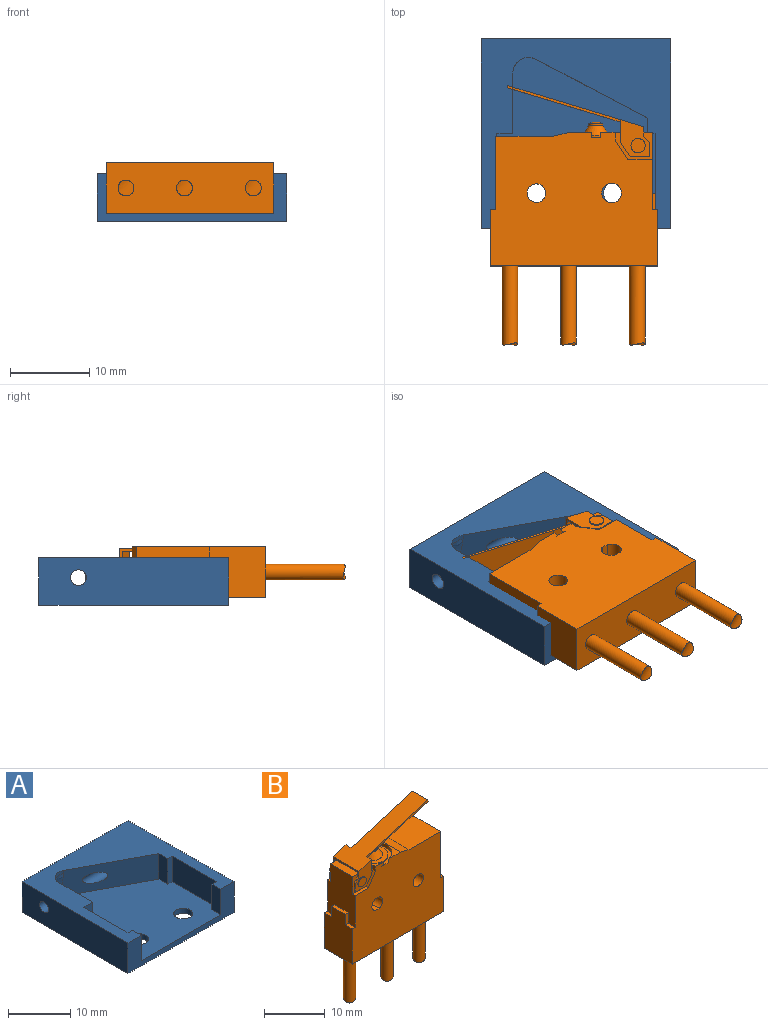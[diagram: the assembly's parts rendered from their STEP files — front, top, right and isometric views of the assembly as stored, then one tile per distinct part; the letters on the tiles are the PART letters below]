
ASSEMBLY  parts=2 mates=1
PART A: 27 faces, bbox 24.8x24.8x7.2 mm
  f0: plane 24x24mm, normal (0,0,1), area 232mm2, adj f4,f5,f6,f10,f11,f12,f13,f14
  f1: cylinder r=1mm len=3mm, axis (1,0,0), area 18.8mm2, adj f4,f22
  f2: cylinder r=1mm len=13.34mm, axis (1,0,0), area 72.3mm2, adj f21,f23
  f3: plane 21.68x20mm, normal (0,0,1), area 329.8mm2, adj f5,f7,f8,f10,f11,f12,f13,f14
  f4: plane 24x6mm, normal (-1,0,0), area 140.9mm2, adj f0,f1,f5,f9,f20
  f5: plane 24x6mm, normal (0,-1,0), area 54mm2, adj f0,f3,f4,f6,f9,f14,f15
  f6: plane 24x6mm, normal (1,0,0), area 131.4mm2, adj f0,f5,f9,f20,f23
  f7: cylinder r=1.5mm len=3mm, axis (0,0,1), area 9.4mm2, adj f3,f9
  f8: cylinder r=1.5mm len=3mm, axis (0,0,1), area 9.4mm2, adj f3,f9
  f9: plane 24x24mm, normal (0,0,-1), area 561.9mm2, adj f4,f5,f6,f7,f8,f20
  f10: plane 5x2mm, normal (-1,0,0), area 10mm2, adj f0,f3,f11,f21
  f11: plane 5x1mm, normal (0,-1,0), area 5mm2, adj f0,f3,f10,f12
  f12: plane 10x5mm, normal (-1,0,0), area 50mm2, adj f0,f3,f11,f13
  f13: plane 5x1mm, normal (0,1,0), area 5mm2, adj f0,f3,f12,f14
  f14: plane 5x2mm, normal (-1,0,0), area 10mm2, adj f0,f3,f5,f13
  f15: plane 5x2mm, normal (1,0,0), area 10mm2, adj f0,f3,f5,f16
  f16: plane 5x1mm, normal (0,1,0), area 5mm2, adj f0,f3,f15,f17
  f17: plane 10x5mm, normal (1,0,0), area 50mm2, adj f0,f3,f16,f18
  f18: plane 5x2mm, normal (0,-1,0), area 10mm2, adj f0,f3,f17,f19
  f19: plane 7.68x5mm, normal (1,0,0), area 29.4mm2, adj f0,f3,f18,f22,f24,f26
  f20: plane 24x6mm, normal (0,1,0), area 144mm2, adj f0,f4,f6,f9
  f21: plane 15.11x8.37mm, normal (-0.47,-0.88,0), area 73.4mm2, adj f0,f2,f3,f10,f24,f25,f26
  f22: torus R=2mm, axis (1,0,0), area 12mm2, adj f1,f19,f25
  f23: torus R=2mm, axis (1,0,0), area 13.5mm2, adj f2,f6
  f24: cylinder r=2mm len=2.94mm, axis (0,0,-1), area 2.5mm2, adj f0,f19,f21,f25
  f25: bspline ~4.52x3.47mm, area 13.7mm2, adj f21,f22,f24,f26
  f26: cylinder r=2mm len=2.94mm, axis (0,0,-1), area 2.5mm2, adj f3,f19,f21,f25
PART B: 76 faces, bbox 21.2x6.4x32.8 mm
  f0: cylinder r=3.25mm len=6.4mm, axis (0,0,1), area 6.3mm2, adj f53,f71,f72,f75
  f1: cylinder r=3.25mm len=6.4mm, axis (0,0,1), area 6.3mm2, adj f53,f63,f71,f75
  f2: cylinder r=0.9mm len=1.8mm, axis (0,0,1), area 1.6mm2, adj f3,f70
  f3: cone r=1.3mm half-angle=33.7deg, axis (0,0,-1), area 11.8mm2, adj f2,f69
  f4: cylinder r=2.6mm len=5.2mm, axis (0,0,1), area 4.9mm2, adj f69,f71
  f5: cylinder r=0.9mm len=1.8mm, axis (0,-1,0), area 0.3mm2, adj f19,f65
  f6: cylinder r=0.9mm len=1.8mm, axis (0,-1,0), area 0.8mm2, adj f18,f57
  f7: cylinder r=1.25mm len=6.4mm, axis (0,1,0), area 19.6mm2, adj f53,f55,f56,f75
  f8: cylinder r=1.25mm len=6.4mm, axis (0,1,0), area 19.6mm2, adj f53,f55,f56,f75
  f9: cylinder r=1.18mm len=6.4mm, axis (0,1,0), area 47.2mm2, adj f53,f75
  f10: cylinder r=2mm len=2.83mm, axis (0.71,-0.71,0), area 2.5mm2, adj f11
  f11: cylinder r=1mm len=10mm, axis (0,0,-1), area 62mm2, adj f10,f52
  f12: cylinder r=2mm len=2.83mm, axis (0.71,-0.71,0), area 2.5mm2, adj f13
  f13: cylinder r=1mm len=10mm, axis (0,0,-1), area 62mm2, adj f12,f52
  f14: cylinder r=2mm len=2.83mm, axis (0.71,-0.71,0), area 2.5mm2, adj f15
  f15: cylinder r=1mm len=10mm, axis (0,0,-1), area 62mm2, adj f14,f52
  f16: cylinder r=0.9mm len=1.8mm, axis (0,-1,0), area 0.8mm2, adj f21,f58
  f17: cylinder r=0.9mm len=1.8mm, axis (0,-1,0), area 0.3mm2, adj f20,f60
  f18: plane 4.69x3.75mm, normal (0,1,0), area 10.6mm2, adj f6,f25,f29,f31,f33,f35,f37,f39
  f19: plane 4.38x3.75mm, normal (0,1,0), area 9.7mm2, adj f5,f28,f30,f32,f34,f36,f38,f39
  f20: plane 4.38x3.75mm, normal (0,-1,0), area 9.7mm2, adj f17,f28,f29,f31,f33,f35,f37,f39
  f21: plane 4.69x3.75mm, normal (0,-1,0), area 10.6mm2, adj f16,f25,f30,f32,f34,f36,f38,f39
  f22: plane 14.29x4.62mm, normal (0,1,0), area 4.5mm2, adj f23,f24,f25,f27,f28,f37
  f23: plane 12.4x3.76mm, normal (0.29,0,-0.96), area 46.6mm2, adj f22,f24,f26,f27
  f24: plane 3.6x0.29mm, normal (0.96,0,0.29), area 1.1mm2, adj f22,f23,f25,f26
  f25: plane 17.15x5.9mm, normal (-0.29,0,0.96), area 71.6mm2, adj f18,f21,f22,f24,f26,f37,f38,f39
  f26: plane 14.29x4.62mm, normal (0,-1,0), area 4.5mm2, adj f23,f24,f25,f27,f28,f38
  f27: plane 3.6x0mm, normal (-0.96,0,-0.29), area 0mm2, adj f22,f23,f26,f28
  f28: plane 5.3x4.84mm, normal (0.29,0,-0.96), area 23.5mm2, adj f19,f20,f22,f26,f27,f37,f38,f39
  f29: plane 0.8x0.8mm, normal (-0.71,0,0.71), area 0.3mm2, adj f18,f20,f31,f39
  f30: plane 0.8x0.8mm, normal (-0.71,0,0.71), area 0.3mm2, adj f19,f21,f32,f39
  f31: plane 1.8x0.3mm, normal (-1,0,0), area 0.5mm2, adj f18,f20,f29,f33
  f32: plane 1.8x0.3mm, normal (-1,0,0), area 0.5mm2, adj f19,f21,f30,f34
  f33: plane 2.5x0.3mm, normal (0,0,-1), area 0.7mm2, adj f18,f20,f31,f35
  f34: plane 2.5x0.3mm, normal (0,0,-1), area 0.7mm2, adj f19,f21,f32,f36
  f35: plane 1.79x1.25mm, normal (0.82,0,-0.57), area 0.7mm2, adj f18,f20,f33,f37
  f36: plane 1.79x1.25mm, normal (0.82,0,-0.57), area 0.7mm2, adj f19,f21,f34,f38
  f37: plane 2.91x1.15mm, normal (1,0,0), area 1.1mm2, adj f18,f20,f22,f25,f28,f35
  f38: plane 2.91x1.15mm, normal (1,0,0), area 1.1mm2, adj f19,f21,f25,f26,f28,f36
  f39: plane 5.9x1.2mm, normal (-1,0,0), area 2.4mm2, adj f18,f19,f20,f21,f25,f28,f29,f30
  f40: plane 2.1x0.7mm, normal (0,-1,0), area 1.5mm2, adj f41,f46,f51,f64
  f41: plane 3.2x0.7mm, normal (0,0,1), area 2.2mm2, adj f40,f42,f51,f64
  f42: plane 2.1x0.7mm, normal (0,1,0), area 1.5mm2, adj f41,f43,f51,f64
  f43: plane 1.6x0.7mm, normal (0,0,1), area 1.1mm2, adj f42,f51,f64,f75
  f44: plane 1.6x0.7mm, normal (0,0,1), area 1.1mm2, adj f47,f50,f54,f75
  f45: plane 1.6x0.7mm, normal (0,0,1), area 1.1mm2, adj f48,f50,f53,f54
  f46: plane 1.6x0.7mm, normal (0,0,1), area 1.1mm2, adj f40,f51,f53,f64
  f47: plane 2.1x0.7mm, normal (0,1,0), area 1.5mm2, adj f44,f49,f50,f54
  f48: plane 2.1x0.7mm, normal (0,-1,0), area 1.5mm2, adj f45,f49,f50,f54
  f49: plane 3.2x0.7mm, normal (0,0,1), area 2.2mm2, adj f47,f48,f50,f54
  f50: plane 9.2x6.4mm, normal (1,0,0), area 52.2mm2, adj f44,f45,f47,f48,f49,f52,f53,f75
  f51: plane 9.2x6.4mm, normal (-1,0,0), area 52.2mm2, adj f40,f41,f42,f43,f46,f52,f53,f75
  f52: plane 21.2x6.4mm, normal (0,0,-1), area 126.3mm2, adj f11,f13,f15,f50,f51,f53,f75
  f53: plane 21.2x16.9mm, normal (0,-1,0), area 316mm2, adj f0,f1,f7,f8,f9,f45,f46,f50
  f54: plane 9.3x6.4mm, normal (1,0,0), area 52.8mm2, adj f44,f45,f47,f48,f49,f53,f74,f75
  f55: plane 6.4x0.85mm, normal (0,0,1), area 5.5mm2, adj f7,f8,f53,f75
  f56: plane 6.4x0.85mm, normal (0,0,-1), area 5.5mm2, adj f7,f8,f53,f75
  f57: plane 1.8x1.8mm, normal (0,1,0), area 2.5mm2, adj f6
  f58: plane 1.8x1.8mm, normal (0,-1,0), area 2.5mm2, adj f16
  f59: plane 1x0.6mm, normal (-1,0,0), area 0.6mm2, adj f60,f61,f63,f75
  f60: plane 4.7x3.5mm, normal (0,1,0), area 11.9mm2, adj f17,f59,f61,f62,f63,f64
  f61: plane 2.5x1.6mm, normal (-0.84,0,0.54), area 1.8mm2, adj f59,f60,f62,f75
  f62: plane 3.1x0.6mm, normal (0,0,1), area 1.9mm2, adj f60,f61,f64,f75
  f63: plane 6.58x6.4mm, normal (0,0,1), area 23.6mm2, adj f1,f53,f59,f60,f64,f65,f66,f75
  f64: plane 9.8x6.4mm, normal (-1,0,0), area 51.8mm2, adj f40,f41,f42,f43,f46,f53,f60,f62
  f65: plane 4.7x3.5mm, normal (0,-1,0), area 11.9mm2, adj f5,f63,f64,f66,f67,f68
  f66: plane 1x0.6mm, normal (-1,0,0), area 0.6mm2, adj f53,f63,f65,f67
  f67: plane 2.5x1.6mm, normal (-0.84,0,0.54), area 1.8mm2, adj f53,f65,f66,f68
  f68: plane 3.1x0.6mm, normal (0,0,1), area 1.9mm2, adj f53,f64,f65,f67
  f69: plane 5.2x5.2mm, normal (0,0,1), area 12.2mm2, adj f3,f4
  f70: sphere r=2mm, area 2.7mm2, adj f2
  f71: plane 6.5x6.4mm, normal (0,0,1), area 11.9mm2, adj f0,f1,f4,f53,f75
  f72: plane 6.4x2.78mm, normal (0,0,1), area 4.9mm2, adj f0,f53,f73,f75
  f73: plane 6.4x2mm, normal (0.24,0,0.97), area 13.2mm2, adj f53,f72,f74,f75
  f74: plane 7.3x6.4mm, normal (0,0,1), area 46.7mm2, adj f53,f54,f73,f75
  f75: plane 21.2x16.9mm, normal (0,1,0), area 316mm2, adj f0,f1,f7,f8,f9,f43,f44,f50
PLACE A t=(-4.68,-4.83,2.31)mm
PLACE B rot(axis=(0,0.71,0.71),180deg) t=(-4.93,-10.23,5.51)mm
MATE fastened B.f9 <-> A.f8  axis (0,0,-1) through (-9.68,-7.33,2.31)mm
